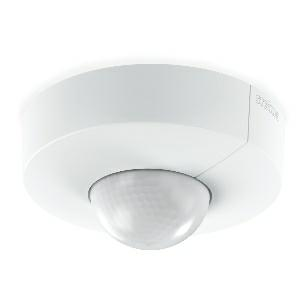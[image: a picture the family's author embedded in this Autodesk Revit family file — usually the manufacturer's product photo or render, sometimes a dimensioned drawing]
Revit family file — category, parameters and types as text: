
# Revit family: is_345_058272
name_source: partatom
category: Elektroinstallationen
revit_build: Autodesk Revit 2016 (Build: 20190508_0715(x64)
units: mm (PartAtom-declared; Revit-internal decimal feet)

## family parameters
Basisbauteil = Fläche
Beim Laden mit Abzugskörper schneiden = Nein
Bemaßung runder Anschluss = Durchmesser verwenden
Beschriftungsausrichtung beibehalten = Nein
Gemeinsam genutzt = Nein
Raumberechnungspunkt = Nein
Teiletyp = Normal

## types (1)
- IS 345
    Apparent Load = 0 VA
    Beschreibung = Type: Motion detectors; Dimensions (Ø x H): 126 x 65 mm; Sensor Technology: passive infrared; Application, place: Outdoors, Indoors; Application, room: corridor / aisle, multi-storey / underground car park, outdoors, Indoors; Installation site: ceiling; Installation: Surface wiring; Electronic scalability: No; Mechanical scalability: No; Mounting height: 2,50 – 5,00 m; Optimum mounting height: 2,5 m; Detection angle: 360 °; Angle of aperture: 45 °; Sneak-by guard: Yes; Capability of masking out individual segments: Yes; Reach, radial: 12 x 6 m (72 m²); Reach, tangential: 23 x 6 m (138 m²); Twilight setting TEACH: Yes; Time setting: 0 sec – 1092 min; Basic light level function: Yes; KNX functions: Photo-cell controller, Basic light level function, Light level, HVAC output, Constant-lighting control, Light output 2x, Presence output, Day / night function; With bus coupling: Yes; Settings via: ETS software, Remote control, Bus, Smart Remote; IP-rating: IP54; Material: Plastic; Colour: white; Version: KNX - surface, rd.; PU1, EAN: 4007841058272
    Height = 0 mm  [stored 0 ft]
    Hersteller = Steinel
    Length = 126 mm
    Maximum range = 11.589 m
    ModVariant = Nein
    Modell = 058272
    Mounting Place = Ceiling
    Mounting Type = Surface mounted
    Number of Poles = 1
    OnlyDefault = Ja
    Power Factor = 1
    Product Name = IS 345
    Product group = Sensor-switched outdoor light
    ProductGroupID = 3
    Protection Class = Protection class
    Protection Degree = IP 54
    RlxData = <blob elided: 155797 chars, md5=5f993bc2>
    Sensor characteristics = Stretched
    Sensor type = Passive (infrared)
    SensorDataFile = <blob elided: 5885 chars, md5=98bccc25>
    Type of entry = Motion
    Typenbild = produkt1_058272.jpg
    Typenkommentare = Product without accessories
    URL = http://relux.com
    VarID = ---
    Voltage = 0 V
    Vorgabe-Ansicht = 1800 mm
    Weight = 0.00 kg
    Width = 0 mm  [stored 0 ft]

note: [stored X ft] marks values corroborated as IEEE doubles in the binary element streams (Revit-internal decimal feet)

## geometry (parser evidence)
native form markers: Blend x4, Sweep x20
no freeform markers — native parametric forms only
